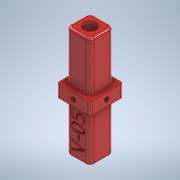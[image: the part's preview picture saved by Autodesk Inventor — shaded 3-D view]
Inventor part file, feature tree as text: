
AUTODESK INVENTOR PART (.ipt)
format: ipt  version: 2020 (Build 240168000, 168)  size: 266,752 bytes
history: native  units: in
note: dims shown in document units (in); Inventor stores cm internally (conversion verified against a paired STEP export)
features: sketch x8, hole x5, fillet x4, extrude x3
ambient origin geometry x8: Origin, YZ Plane, XZ Plane, XY Plane, X Axis, Y Axis, Z Axis, Center Point
bodies: Solid1 (feature_tree)
feature tree (20):
  extrude  "CenterPortion"  TaperAngle=0.0deg  [1 undecoded]
  extrude  "OuterPortion"  Depth=0.8108in
  extrude  "TextWithVersionNumber"  Depth=0.8108in
  hole  "CenterSupportHole"  [1 undecoded]
  fillet  "Fillet1"  [1 undecoded]
  fillet  "Fillet2"  [1 undecoded]
  sketch  "Sketch5"  dims[d29=0.12in d30=0.2913in d31=0.375in d32=0.25in d33=0.5635in d35=0.8108in]
  sketch  "Sketch6"  dims[d36=0.12in d37=0.2913in d38=0.375in d39=0.25in d40=0.5635in d41=0.5in d42=0.8108in]
  sketch  "Sketch7"  dims[d43=0.12in d44=0.2913in d45=0.375in d46=0.25in d47=0.5635in d48=0.5in d49=0.8108in]
  sketch  "Sketch8"
  hole  "Hole2"  [1 undecoded]
  hole  "Hole3"  [1 undecoded]
  hole  "Hole4"  [1 undecoded]
  hole  "Hole5"  [1 undecoded]
  fillet  "BottomFillet"  [1 undecoded]
  fillet  "TopFille"  [1 undecoded]
  sketch  "Sketch1"  dims[d3=0.0in d7=0.0in]
  sketch  "Sketch2"  dims[d12=0.0in]
  sketch  "Sketch3"  dims[d14=0.75in d15=0.375in d16=0.25in d17=0.5635in d18=1.0in d19=0.8108in]
  sketch  "Sketch4"  dims[d22=0.12in d23=0.2913in d24=0.375in d25=0.25in d26=0.5635in d28=0.8108in]
note: 10 required parameter values undecoded (feature->parameter linkage not recoverable at this tier; creation-order binding heuristic only, values carry confidence <= 0.55)
